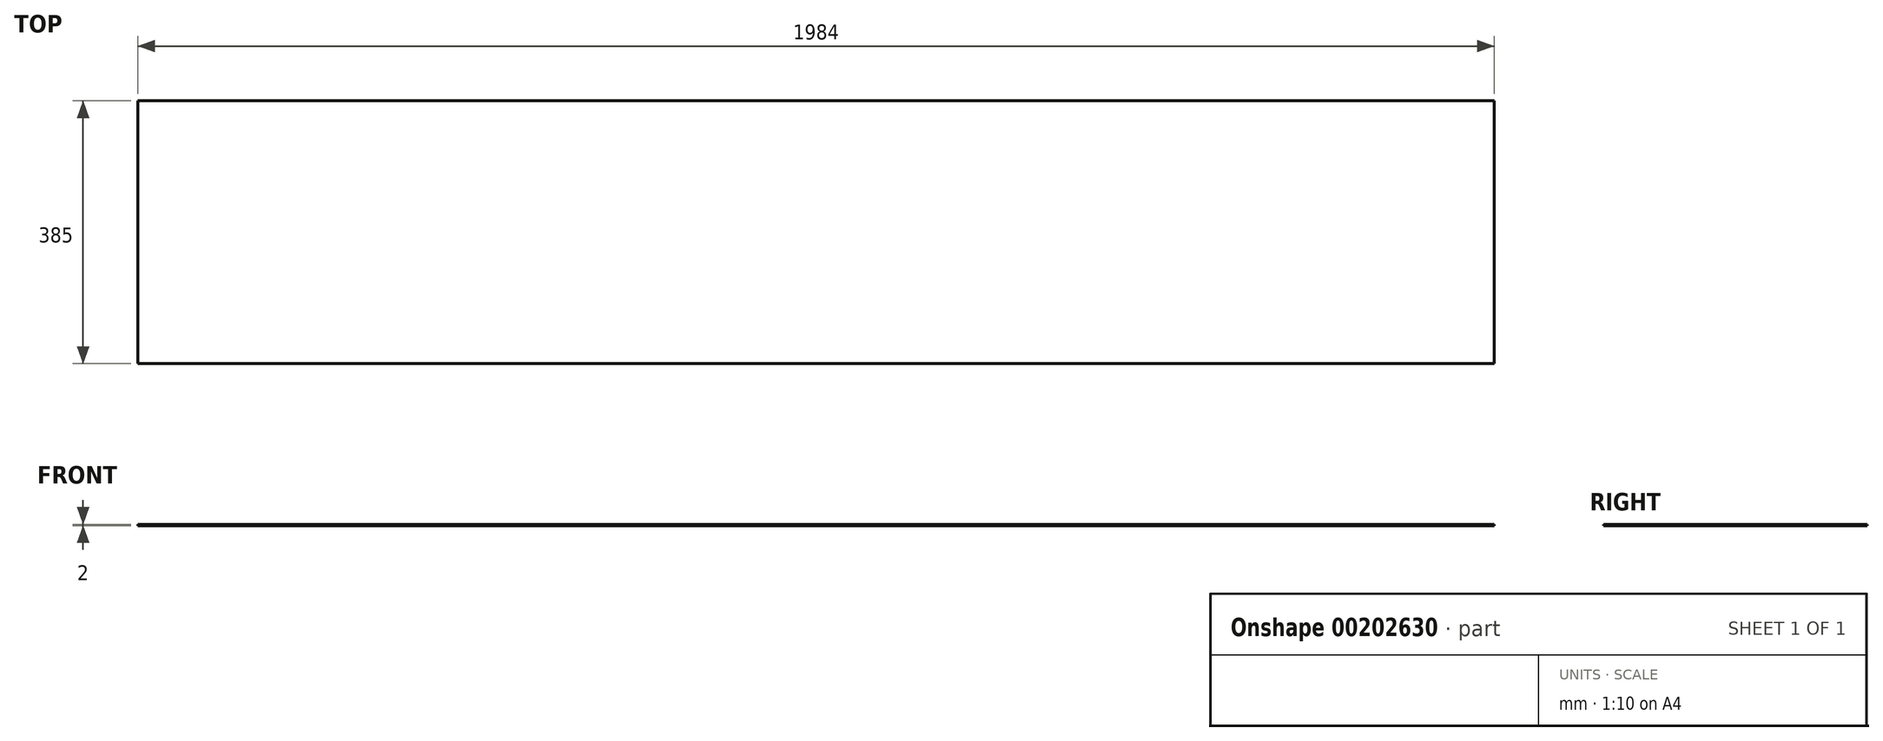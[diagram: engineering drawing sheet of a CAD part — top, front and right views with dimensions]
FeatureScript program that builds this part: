
annotation { "Feature Type Name" : "Feature", "Feature Type Description" : "" }
export const myFeature = defineFeature(function(context is Context, id is Id, definition is map)
    precondition{}
    {
        {
            var Q0;
            Q0=qCreatedBy(makeId("Top.planeOp"),FACE);
            var sketch = newSketch(context, id + "F0", { "sketchPlane" : qUnion([Q0])});
            skLineSegment(sketch, "E0.bottom", {"start": v(-864.34, -235.28) * mm, "end": v(1119.66, -235.28) * mm});
            skLineSegment(sketch, "E0.top", {"start": v(-864.34, 149.72) * mm, "end": v(1119.66, 149.72) * mm});
            skLineSegment(sketch, "E0.left", {"start": v(-864.34, -235.28) * mm, "end": v(-864.34, 149.72) * mm});
            skLineSegment(sketch, "E0.right", {"start": v(1119.66, -235.28) * mm, "end": v(1119.66, 149.72) * mm});
            skSolve(sketch);
        }
        {
            var Q0;
            Q0=makeQuery(id+"F0.imprint","IMPRINT",FACE,{"disambiguationData":[TD([[makeQuery(id+"F0.imprint","IMPRINT",EDGE,{"derivedFrom":sQuery(id+"F0.wireOp",EDGE,"E0.bottom")}),1.0]])]});
            extrude(context, id + "F1", {"entities" : qUnion([Q0]), "depth" : 2 * mm});
        }
    });
